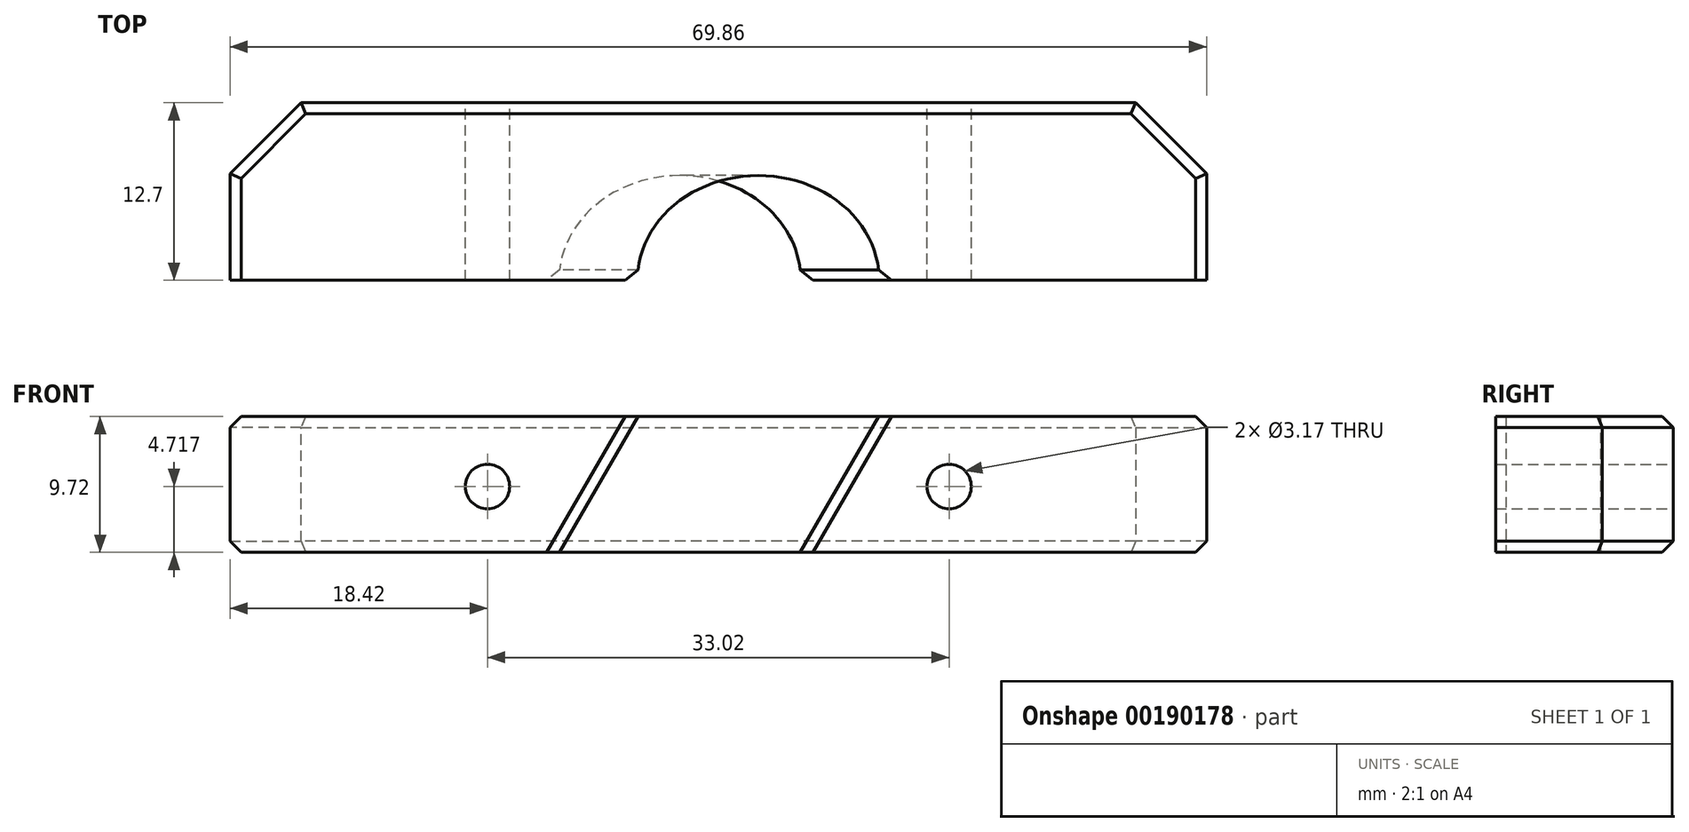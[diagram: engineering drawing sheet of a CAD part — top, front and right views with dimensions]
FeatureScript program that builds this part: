
annotation { "Feature Type Name" : "Feature", "Feature Type Description" : "" }
export const myFeature = defineFeature(function(context is Context, id is Id, definition is map)
    precondition{}
    {
        {
            var Q0;
            Q0=qCreatedBy(makeId("Top.planeOp"),FACE);
            var sketch = newSketch(context, id + "F0", { "sketchPlane" : qUnion([Q0])});
            skLineSegment(sketch, "E0", {"start": v(0, 0) * mm, "end": v(-34.93, 0) * mm});
            skLineSegment(sketch, "E1", {"start": v(-34.93, 0) * mm, "end": v(-34.93, 12.7) * mm});
            skLineSegment(sketch, "E2", {"start": v(-34.93, 12.7) * mm, "end": v(0, 12.7) * mm});
            skLineSegment(sketch, "E3", {"start": v(0, 12.7) * mm, "end": v(0, 0) * mm});
            skLineSegment(sketch, "E4.MirrorCS", {"start": v(34.93, 12.7) * mm, "end": v(0, 12.7) * mm});
            skLineSegment(sketch, "E5.MirrorCS", {"start": v(0, 0) * mm, "end": v(34.93, 0) * mm});
            skLineSegment(sketch, "E6.MirrorCS", {"start": v(34.93, 0) * mm, "end": v(34.93, 12.7) * mm});
            skSolve(sketch);
        }
        {
            var Q0;
            Q0=qSketchRegion(id+"F0",true);
            extrude(context, id + "F1", {"entities" : qUnion([Q0]), "depth" : 9.72 * mm});
        }
        {
            var Q0;
            Q0=makeQuery(id+"F1.opExtrude","CAP_FACE",FACE,{"disambiguationData":[OSD([sQuery(id+"F0.wireOp",EDGE,"E0"),sQuery(id+"F0.wireOp",EDGE,"E1"),sQuery(id+"F0.wireOp",EDGE,"E2"),sQuery(id+"F0.wireOp",EDGE,"E4.MirrorCS"),sQuery(id+"F0.wireOp",EDGE,"E5.MirrorCS"),sQuery(id+"F0.wireOp",EDGE,"E6.MirrorCS")])],"isStart":false});
            var sketch = newSketch(context, id + "F2", { "sketchPlane" : qUnion([Q0])});
            skCircle(sketch, "E7", {"center": v(0, 0) * mm, "radius": 7.62 * mm});
            skSolve(sketch);
        }
        {
            var Q0;
            Q0=makeQuery(id+"F1.opExtrude","SWEPT_FACE",FACE,{"disambiguationData":[OSD([sQuery(id+"F0.wireOp",EDGE,"E2"),sQuery(id+"F0.wireOp",EDGE,"E4.MirrorCS")])]});
            var sketch = newSketch(context, id + "F3", { "sketchPlane" : qUnion([Q0])});
            skCircle(sketch, "E8", {"center": v(16.51, 4.72) * mm, "radius": 1.59 * mm});
            skCircle(sketch, "E9.MirrorC", {"center": v(-16.51, 4.72) * mm, "radius": 1.59 * mm});
            skSolve(sketch);
        }
        {
            var Q0;
            Q0=qSketchRegion(id+"F3",true);
            extrude(context, id + "F4", {"entities" : qUnion([Q0]), "operationType" : NewBodyOperationType.REMOVE, "oppositeDirection" : true, "depth" : 25.4 * mm});
        }
        {
            var Q0;
            Q0=makeQuery(id+"F1.opExtrude","CAP_EDGE",EDGE,{"disambiguationData":[OSD([sQuery(id+"F0.wireOp",EDGE,"E1")])],"isStart":false});
            var Q1;
            Q1=makeQuery(id+"F1.opExtrude","CAP_EDGE",EDGE,{"disambiguationData":[OSD([sQuery(id+"F0.wireOp",EDGE,"E6.MirrorCS")])],"isStart":false});
            var Q2;
            Q2=makeQuery(id+"F1.opExtrude","CAP_EDGE",EDGE,{"disambiguationData":[OSD([sQuery(id+"F0.wireOp",EDGE,"E2"),sQuery(id+"F0.wireOp",EDGE,"E4.MirrorCS")])],"isStart":false});
            var Q3;
            Q3=makeQuery(id+"Fnr2OtXorCAfB5X_1.boolean.opBoolean","INTERSECT",EDGE,{"disambiguationData":[OD(1.0)],"derivedFrom":[makeQuery(id+"F1.opExtrude","SWEPT_FACE",FACE,{"disambiguationData":[OSD([sQuery(id+"F0.wireOp",EDGE,"E0"),sQuery(id+"F0.wireOp",EDGE,"E5.MirrorCS")])]}),makeQuery(id+"Fnr2OtXorCAfB5X_1.opExtrude","SWEPT_FACE",FACE,{"disambiguationData":[OSD([sQuery(id+"F2.wireOp",EDGE,"E7")])]})]});
            var Q4;
            Q4=makeQuery(id+"Fnr2OtXorCAfB5X_1.boolean.opBoolean","INTERSECT",EDGE,{"disambiguationData":[OD(0.0)],"derivedFrom":[makeQuery(id+"F1.opExtrude","SWEPT_FACE",FACE,{"disambiguationData":[OSD([sQuery(id+"F0.wireOp",EDGE,"E0"),sQuery(id+"F0.wireOp",EDGE,"E5.MirrorCS")])]}),makeQuery(id+"Fnr2OtXorCAfB5X_1.opExtrude","SWEPT_FACE",FACE,{"disambiguationData":[OSD([sQuery(id+"F2.wireOp",EDGE,"E7")])]})]});
            var Q5;
            Q5=makeQuery(id+"F1.opExtrude","CAP_EDGE",EDGE,{"disambiguationData":[OSD([sQuery(id+"F0.wireOp",EDGE,"E2"),sQuery(id+"F0.wireOp",EDGE,"E4.MirrorCS")])],"isStart":true});
            var Q6;
            Q6=makeQuery(id+"F1.opExtrude","CAP_EDGE",EDGE,{"disambiguationData":[OSD([sQuery(id+"F0.wireOp",EDGE,"E1")])],"isStart":true});
            var Q7;
            Q7=makeQuery(id+"F1.opExtrude","CAP_EDGE",EDGE,{"disambiguationData":[OSD([sQuery(id+"F0.wireOp",EDGE,"E6.MirrorCS")])],"isStart":true});
            var Q8;
            Q8=makeQuery(id+"Fnr2OtXorCAfB5X_1.boolean.opBoolean","COPY",EDGE,{"derivedFrom":makeQuery(id+"Fnr2OtXorCAfB5X_1.opExtrude","CAP_EDGE",EDGE,{"disambiguationData":[OSD([sQuery(id+"F2.wireOp",EDGE,"E7")])],"isStart":true})});
            var Q9;
            Q9=makeQuery(id+"Fnr2OtXorCAfB5X_1.boolean.opBoolean","INTERSECT",EDGE,{"derivedFrom":[makeQuery(id+"F1.opExtrude","CAP_FACE",FACE,{"disambiguationData":[OSD([sQuery(id+"F0.wireOp",EDGE,"E0"),sQuery(id+"F0.wireOp",EDGE,"E1"),sQuery(id+"F0.wireOp",EDGE,"E2"),sQuery(id+"F0.wireOp",EDGE,"E4.MirrorCS"),sQuery(id+"F0.wireOp",EDGE,"E5.MirrorCS"),sQuery(id+"F0.wireOp",EDGE,"E6.MirrorCS")])],"isStart":true}),makeQuery(id+"Fnr2OtXorCAfB5X_1.opExtrude","SWEPT_FACE",FACE,{"disambiguationData":[OSD([sQuery(id+"F2.wireOp",EDGE,"E7")])]})]});
            chamfer(context, id + "F5", {"entities" : qUnion([Q0, Q1, Q2, Q3, Q4, Q5, Q6, Q7, Q8, Q9]), "width" : 0.8 * mm, "tangentPropagation" : true});
        }
        {
            var Q0;
            Q0=makeQuery(id+"F1.opExtrude","SWEPT_EDGE",EDGE,{"disambiguationData":[OSD([sQuery(id+"F0.wireOp",EDGE,"E4.MirrorCS"),sQuery(id+"F0.wireOp",EDGE,"E6.MirrorCS")])]});
            var Q1;
            Q1=makeQuery(id+"F1.opExtrude","SWEPT_EDGE",EDGE,{"disambiguationData":[OSD([sQuery(id+"F0.wireOp",EDGE,"E1"),sQuery(id+"F0.wireOp",EDGE,"E2")])]});
            chamfer(context, id + "F6", {"entities" : qUnion([Q0, Q1]), "width" : 5.08 * mm, "tangentPropagation" : true});
        }
        {
            var Q0;
            {var subQ0=sQuery(id+"F0.wireOp",EDGE,"E6.MirrorCS");var subQ1=sQuery(id+"F0.wireOp",EDGE,"E4.MirrorCS");Q0=makeQuery(id+"F6.opChamfer","BLEND_EDGE",EDGE,{"blendedFrom":[makeQuery(id+"F1.opExtrude","SWEPT_EDGE",EDGE,{"disambiguationData":[OSD([subQ1,subQ0])]}),makeQuery(id+"F1.opExtrude","CAP_FACE",FACE,{"disambiguationData":[OSD([sQuery(id+"F0.wireOp",EDGE,"E0"),sQuery(id+"F0.wireOp",EDGE,"E1"),sQuery(id+"F0.wireOp",EDGE,"E2"),subQ1,sQuery(id+"F0.wireOp",EDGE,"E5.MirrorCS"),subQ0])],"isStart":true})],"blendedInto":[makeQuery(id+"F1.opExtrude","CAP_FACE",FACE,{"disambiguationData":[OSD([sQuery(id+"F0.wireOp",EDGE,"E0"),sQuery(id+"F0.wireOp",EDGE,"E1"),sQuery(id+"F0.wireOp",EDGE,"E2"),subQ1,sQuery(id+"F0.wireOp",EDGE,"E5.MirrorCS"),subQ0])],"isStart":true})]});}
            var Q1;
            {var subQ0=sQuery(id+"F0.wireOp",EDGE,"E6.MirrorCS");var subQ1=sQuery(id+"F0.wireOp",EDGE,"E4.MirrorCS");Q1=makeQuery(id+"F6.opChamfer","BLEND_EDGE",EDGE,{"blendedFrom":[makeQuery(id+"F1.opExtrude","SWEPT_EDGE",EDGE,{"disambiguationData":[OSD([subQ1,subQ0])]}),makeQuery(id+"F1.opExtrude","CAP_FACE",FACE,{"disambiguationData":[OSD([sQuery(id+"F0.wireOp",EDGE,"E0"),sQuery(id+"F0.wireOp",EDGE,"E1"),sQuery(id+"F0.wireOp",EDGE,"E2"),subQ1,sQuery(id+"F0.wireOp",EDGE,"E5.MirrorCS"),subQ0])],"isStart":false})],"blendedInto":[makeQuery(id+"F1.opExtrude","CAP_FACE",FACE,{"disambiguationData":[OSD([sQuery(id+"F0.wireOp",EDGE,"E0"),sQuery(id+"F0.wireOp",EDGE,"E1"),sQuery(id+"F0.wireOp",EDGE,"E2"),subQ1,sQuery(id+"F0.wireOp",EDGE,"E5.MirrorCS"),subQ0])],"isStart":false})]});}
            var Q2;
            {var subQ0=sQuery(id+"F0.wireOp",EDGE,"E2");var subQ1=sQuery(id+"F0.wireOp",EDGE,"E1");Q2=makeQuery(id+"F6.opChamfer","BLEND_EDGE",EDGE,{"blendedFrom":[makeQuery(id+"F1.opExtrude","SWEPT_EDGE",EDGE,{"disambiguationData":[OSD([subQ1,subQ0])]}),makeQuery(id+"F1.opExtrude","CAP_FACE",FACE,{"disambiguationData":[OSD([sQuery(id+"F0.wireOp",EDGE,"E0"),subQ1,subQ0,sQuery(id+"F0.wireOp",EDGE,"E4.MirrorCS"),sQuery(id+"F0.wireOp",EDGE,"E5.MirrorCS"),sQuery(id+"F0.wireOp",EDGE,"E6.MirrorCS")])],"isStart":false})],"blendedInto":[makeQuery(id+"F1.opExtrude","CAP_FACE",FACE,{"disambiguationData":[OSD([sQuery(id+"F0.wireOp",EDGE,"E0"),subQ1,subQ0,sQuery(id+"F0.wireOp",EDGE,"E4.MirrorCS"),sQuery(id+"F0.wireOp",EDGE,"E5.MirrorCS"),sQuery(id+"F0.wireOp",EDGE,"E6.MirrorCS")])],"isStart":false})]});}
            var Q3;
            {var subQ0=sQuery(id+"F0.wireOp",EDGE,"E2");var subQ1=sQuery(id+"F0.wireOp",EDGE,"E1");Q3=makeQuery(id+"F6.opChamfer","BLEND_EDGE",EDGE,{"blendedFrom":[makeQuery(id+"F1.opExtrude","SWEPT_EDGE",EDGE,{"disambiguationData":[OSD([subQ1,subQ0])]}),makeQuery(id+"F1.opExtrude","CAP_FACE",FACE,{"disambiguationData":[OSD([sQuery(id+"F0.wireOp",EDGE,"E0"),subQ1,subQ0,sQuery(id+"F0.wireOp",EDGE,"E4.MirrorCS"),sQuery(id+"F0.wireOp",EDGE,"E5.MirrorCS"),sQuery(id+"F0.wireOp",EDGE,"E6.MirrorCS")])],"isStart":true})],"blendedInto":[makeQuery(id+"F1.opExtrude","CAP_FACE",FACE,{"disambiguationData":[OSD([sQuery(id+"F0.wireOp",EDGE,"E0"),subQ1,subQ0,sQuery(id+"F0.wireOp",EDGE,"E4.MirrorCS"),sQuery(id+"F0.wireOp",EDGE,"E5.MirrorCS"),sQuery(id+"F0.wireOp",EDGE,"E6.MirrorCS")])],"isStart":true})]});}
            chamfer(context, id + "F7", {"entities" : qUnion([Q0, Q1, Q2, Q3]), "width" : 0.8 * mm, "tangentPropagation" : true});
        }
        {
            var Q0;
            Q0=qCreatedBy(makeId("Top.planeOp"),FACE);
            var Q1;
            {var subQ0=sQuery(id+"F0.wireOp",EDGE,"E6.MirrorCS");Q1=makeQuery(id+"F5.opChamfer","BLEND_EDGE",EDGE,{"blendedFrom":[makeQuery(id+"F1.opExtrude","CAP_EDGE",EDGE,{"disambiguationData":[OSD([subQ0])],"isStart":true}),makeQuery(id+"F1.opExtrude","CAP_FACE",FACE,{"disambiguationData":[OSD([sQuery(id+"F0.wireOp",EDGE,"E0"),sQuery(id+"F0.wireOp",EDGE,"E1"),sQuery(id+"F0.wireOp",EDGE,"E2"),sQuery(id+"F0.wireOp",EDGE,"E4.MirrorCS"),sQuery(id+"F0.wireOp",EDGE,"E5.MirrorCS"),subQ0])],"isStart":true})],"blendedInto":[makeQuery(id+"F1.opExtrude","CAP_FACE",FACE,{"disambiguationData":[OSD([sQuery(id+"F0.wireOp",EDGE,"E0"),sQuery(id+"F0.wireOp",EDGE,"E1"),sQuery(id+"F0.wireOp",EDGE,"E2"),sQuery(id+"F0.wireOp",EDGE,"E4.MirrorCS"),sQuery(id+"F0.wireOp",EDGE,"E5.MirrorCS"),subQ0])],"isStart":true})]});}
            cPlane(context, id + "F8", {"entities" : qUnion([Q0, Q1]), "cplaneType" : CPlaneType.LINE_ANGLE, "offset" : 25.4 * mm, "angle" : 30 * degree, "width" : 152.4 * mm, "height" : 152.4 * mm});
        }
        {
            var Q0;
            Q0=qCreatedBy(id+"F8.planeOp",FACE);
            var sketch = newSketch(context, id + "F9", { "sketchPlane" : qUnion([Q0])});
            skCircle(sketch, "E10", {"center": v(2.38, 0) * mm, "radius": 7.5 * mm});
            skSolve(sketch);
        }
        {
            var Q0;
            {var subQ0=sQuery(id+"F0.wireOp",EDGE,"E1");Q0=makeQuery(id+"F5.opChamfer","BLEND_EDGE",EDGE,{"blendedFrom":[makeQuery(id+"F1.opExtrude","CAP_EDGE",EDGE,{"disambiguationData":[OSD([subQ0])],"isStart":true}),makeQuery(id+"F1.opExtrude","SWEPT_FACE",FACE,{"disambiguationData":[OSD([subQ0])]})],"blendedInto":[makeQuery(id+"F1.opExtrude","SWEPT_FACE",FACE,{"disambiguationData":[OSD([subQ0])]})]});}
            cPlane(context, id + "F10", {"entities" : qUnion([Q0]), "cplaneType" : CPlaneType.LINE_ANGLE, "offset" : 25.4 * mm, "angle" : 150 * degree, "width" : 152.4 * mm, "height" : 152.4 * mm});
        }
        {
            var Q0;
            Q0=qCreatedBy(id+"F10.planeOp",FACE);
            var sketch = newSketch(context, id + "F11", { "sketchPlane" : qUnion([Q0])});
            skCircle(sketch, "E11", {"center": v(-2.38, 0) * mm, "radius": 7.5 * mm});
            skSolve(sketch);
        }
        {
            var Q0;
            Q0 = qSketchRegion(id + "F11", true);
            extrude(context, id + "F12", {"entities" : qUnion([Q0]), "operationType" : NewBodyOperationType.REMOVE, "depth" : 50.8 * mm});
        }
        {
            var Q0;
            Q0=makeQuery(id+"F12.boolean.opBoolean","INTERSECT",EDGE,{"disambiguationData":[OD(0.0)],"derivedFrom":[makeQuery(id+"F1.opExtrude","SWEPT_FACE",FACE,{"disambiguationData":[OSD([sQuery(id+"F0.wireOp",EDGE,"E0"),sQuery(id+"F0.wireOp",EDGE,"E5.MirrorCS")])]}),makeQuery(id+"F12.opExtrude","SWEPT_FACE",FACE,{"disambiguationData":[OSD([sQuery(id+"F11.wireOp",EDGE,"E11")])]})]});
            var Q1;
            Q1=makeQuery(id+"F12.boolean.opBoolean","INTERSECT",EDGE,{"disambiguationData":[OD(1.0)],"derivedFrom":[makeQuery(id+"F1.opExtrude","SWEPT_FACE",FACE,{"disambiguationData":[OSD([sQuery(id+"F0.wireOp",EDGE,"E0"),sQuery(id+"F0.wireOp",EDGE,"E5.MirrorCS")])]}),makeQuery(id+"F12.opExtrude","SWEPT_FACE",FACE,{"disambiguationData":[OSD([sQuery(id+"F11.wireOp",EDGE,"E11")])]})]});
            chamfer(context, id + "F13", {"entities" : qUnion([Q0, Q1]), "width" : 0.8 * mm, "tangentPropagation" : true});
        }
    });
